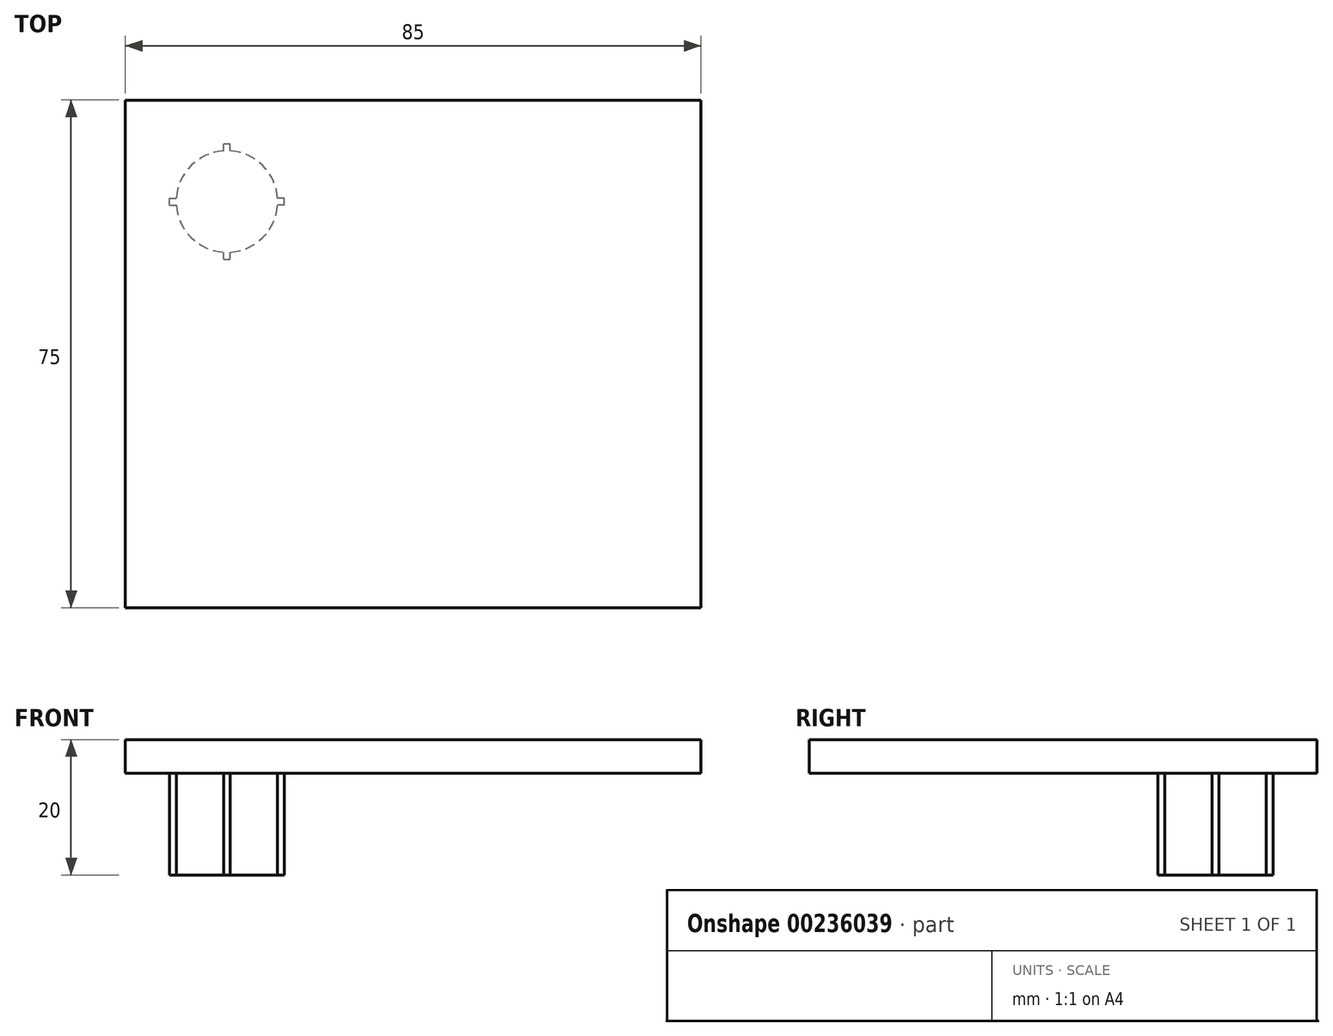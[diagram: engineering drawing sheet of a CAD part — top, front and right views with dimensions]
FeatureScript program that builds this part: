
annotation { "Feature Type Name" : "Feature", "Feature Type Description" : "" }
export const myFeature = defineFeature(function(context is Context, id is Id, definition is map)
    precondition{}
    {
        {
            var Q0;
            Q0=qCreatedBy(makeId("Top.planeOp"),FACE);
            var sketch = newSketch(context, id + "F0", { "sketchPlane" : qUnion([Q0])});
            skLineSegment(sketch, "E0.bottom", {"start": v(-70.04, -31.41) * mm, "end": v(14.96, -31.41) * mm});
            skLineSegment(sketch, "E0.top", {"start": v(-70.04, 43.59) * mm, "end": v(14.96, 43.59) * mm});
            skLineSegment(sketch, "E0.left", {"start": v(-70.04, -31.41) * mm, "end": v(-70.04, 43.59) * mm});
            skLineSegment(sketch, "E0.right", {"start": v(14.96, -31.41) * mm, "end": v(14.96, 43.59) * mm});
            skSolve(sketch);
        }
        {
            var Q0;
            Q0=makeQuery(id+"F0.imprint","IMPRINT",FACE,{"disambiguationData":[TD([[makeQuery(id+"F0.imprint","IMPRINT",EDGE,{"derivedFrom":sQuery(id+"F0.wireOp",EDGE,"E0.bottom")}),1.0]])]});
            extrude(context, id + "F1", {"entities" : qUnion([Q0]), "depth" : 5 * mm});
        }
        {
            var Q0;
            Q0=makeQuery(id+"F1.opExtrude","CAP_FACE",FACE,{"disambiguationData":[OSD([sQuery(id+"F0.wireOp",EDGE,"E0.bottom"),sQuery(id+"F0.wireOp",EDGE,"E0.top"),sQuery(id+"F0.wireOp",EDGE,"E0.left"),sQuery(id+"F0.wireOp",EDGE,"E0.right")])],"isStart":true});
            var sketch = newSketch(context, id + "F2", { "sketchPlane" : qUnion([Q0])});
            skCircle(sketch, "E1", {"center": v(-55.04, -28.59) * mm, "radius": 7.5 * mm});
            skPoint(sketch, "E2.middle", {"position": v(-62.54, -28.59) * mm});
            skPoint(sketch, "E3", {"position": v(-55.04, -21.09) * mm});
            skPoint(sketch, "E4", {"position": v(-55.04, -36.09) * mm});
            skPoint(sketch, "E5", {"position": v(-47.54, -28.59) * mm});
            skLineSegment(sketch, "E6.bottom", {"start": v(-63.54, -28.09) * mm, "end": v(-61.54, -28.09) * mm});
            skLineSegment(sketch, "E6.top", {"start": v(-63.54, -29.09) * mm, "end": v(-61.54, -29.09) * mm});
            skLineSegment(sketch, "E6.left", {"start": v(-63.54, -28.09) * mm, "end": v(-63.54, -29.09) * mm});
            skPoint(sketch, "E7", {"position": v(-62.54, -28.09) * mm});
            skPoint(sketch, "E8", {"position": v(-62.54, -29.09) * mm});
            skLineSegment(sketch, "E9.bottom", {"start": v(-46.54, -28.09) * mm, "end": v(-48.54, -28.09) * mm});
            skLineSegment(sketch, "E9.top", {"start": v(-46.54, -29.09) * mm, "end": v(-48.54, -29.09) * mm});
            skLineSegment(sketch, "E9.left", {"start": v(-46.54, -28.09) * mm, "end": v(-46.54, -29.09) * mm});
            skLineSegment(sketch, "E10.bottom", {"start": v(-55.54, -20.09) * mm, "end": v(-54.54, -20.09) * mm});
            skLineSegment(sketch, "E10.left", {"start": v(-55.54, -20.09) * mm, "end": v(-55.54, -22.09) * mm});
            skLineSegment(sketch, "E10.right", {"start": v(-54.54, -20.09) * mm, "end": v(-54.54, -22.09) * mm});
            skLineSegment(sketch, "E11.top", {"start": v(-54.54, -37.09) * mm, "end": v(-55.54, -37.09) * mm});
            skLineSegment(sketch, "E11.left", {"start": v(-54.54, -35.09) * mm, "end": v(-54.54, -37.09) * mm});
            skLineSegment(sketch, "E11.right", {"start": v(-55.54, -35.09) * mm, "end": v(-55.54, -37.09) * mm});
            skSolve(sketch);
        }
        {
            var Q0;
            {var subQ0=sQuery(id+"F2.wireOp",EDGE,"E1");var subQ4=makeQuery(id+"F2.imprint","INTERSECT",VERTEX,{"derivedFrom":[subQ0,sQuery(id+"F2.wireOp",EDGE,"E10.right")]});Q0=makeQuery(id+"F2.imprint","IMPRINT",FACE,{"disambiguationData":[TD([[makeQuery(id+"F2.imprint","IMPRINT",EDGE,{"disambiguationData":[TD([[subQ4,1.0]])],"derivedFrom":subQ0}),1.0]])]});}
            var Q1;
            {var subQ5=sQuery(id+"F2.wireOp",EDGE,"E6.left");Q1=makeQuery(id+"F2.imprint","IMPRINT",FACE,{"disambiguationData":[TD([[makeQuery(id+"F2.imprint","IMPRINT",EDGE,{"derivedFrom":subQ5}),1.0]])]});}
            var Q2;
            {var subQ5=sQuery(id+"F2.wireOp",EDGE,"E9.left");Q2=makeQuery(id+"F2.imprint","IMPRINT",FACE,{"disambiguationData":[TD([[makeQuery(id+"F2.imprint","IMPRINT",EDGE,{"derivedFrom":subQ5}),-1.0]])]});}
            var Q3;
            {var subQ5=sQuery(id+"F2.wireOp",EDGE,"E10.bottom");Q3=makeQuery(id+"F2.imprint","IMPRINT",FACE,{"disambiguationData":[TD([[makeQuery(id+"F2.imprint","IMPRINT",EDGE,{"derivedFrom":subQ5}),-1.0]])]});}
            var Q4;
            {var subQ5=sQuery(id+"F2.wireOp",EDGE,"E11.top");Q4=makeQuery(id+"F2.imprint","IMPRINT",FACE,{"disambiguationData":[TD([[makeQuery(id+"F2.imprint","IMPRINT",EDGE,{"derivedFrom":subQ5}),-1.0]])]});}
            extrude(context, id + "F3", {"entities" : qUnion([Q0, Q1, Q2, Q3, Q4]), "operationType" : NewBodyOperationType.ADD, "depth" : 15 * mm});
        }
    });
